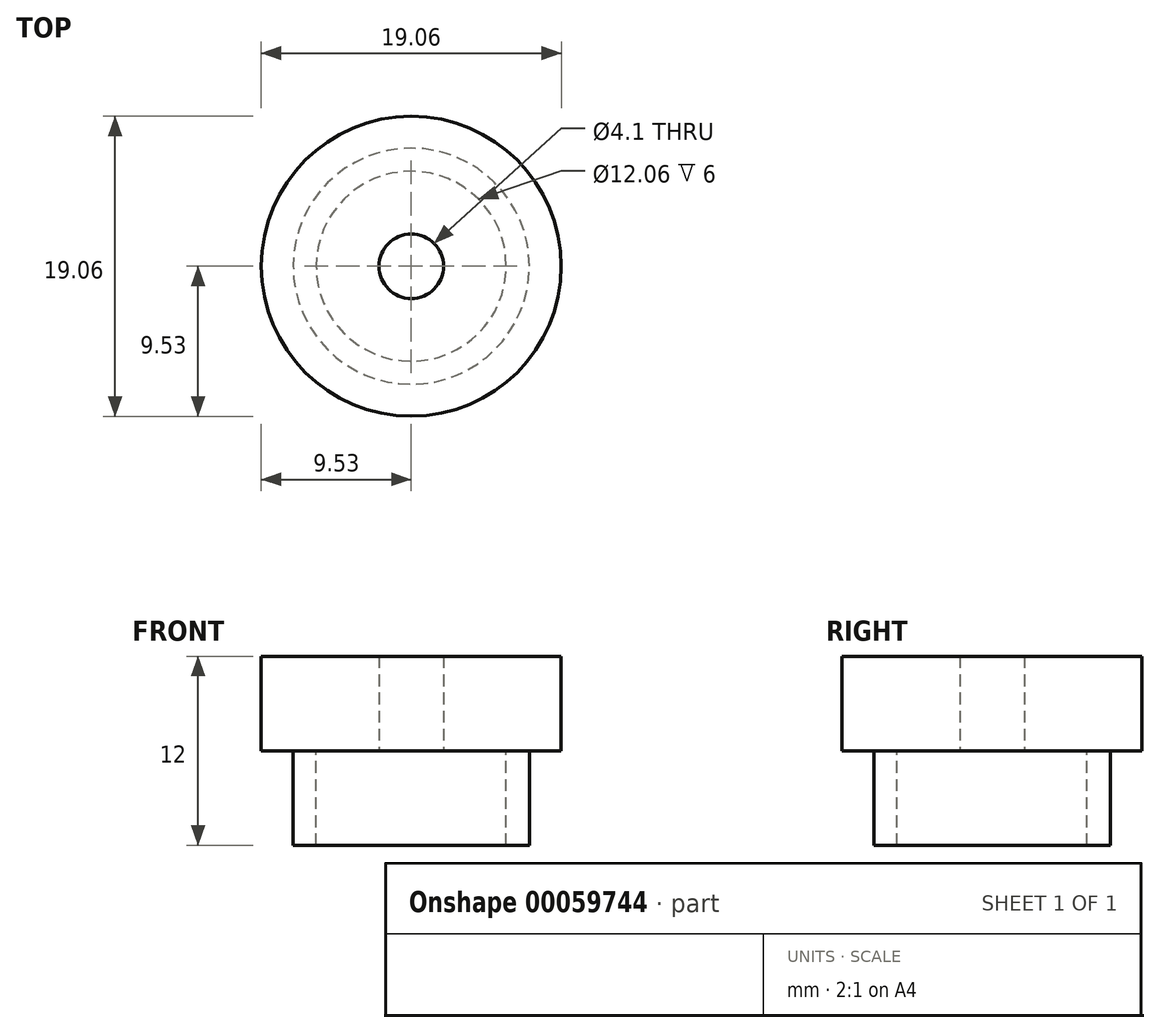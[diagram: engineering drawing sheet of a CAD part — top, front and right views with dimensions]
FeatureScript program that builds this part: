
annotation { "Feature Type Name" : "Feature", "Feature Type Description" : "" }
export const myFeature = defineFeature(function(context is Context, id is Id, definition is map)
    precondition{}
    {
        {
            var Q0;
            Q0=qCreatedBy(makeId("Top.planeOp"),FACE);
            var sketch = newSketch(context, id + "F0", { "sketchPlane" : qUnion([Q0])});
            skCircle(sketch, "E0", {"center": v(0, 0) * mm, "radius": 9.53 * mm});
            skCircle(sketch, "E1", {"center": v(0, 0) * mm, "radius": 7.5 * mm});
            skCircle(sketch, "E2", {"center": v(0, 0) * mm, "radius": 6.03 * mm});
            skCircle(sketch, "E3", {"center": v(0, 0) * mm, "radius": 2.05 * mm});
            skSolve(sketch);
        }
        {
            var Q0;
            Q0=makeQuery(id+"F0.imprint","IMPRINT",FACE,{"disambiguationData":[TD([[makeQuery(id+"F0.imprint","IMPRINT",EDGE,{"derivedFrom":sQuery(id+"F0.wireOp",EDGE,"E0")}),1.0]])]});
            var Q1;
            Q1=makeQuery(id+"F0.imprint","IMPRINT",FACE,{"disambiguationData":[TD([[makeQuery(id+"F0.imprint","IMPRINT",EDGE,{"derivedFrom":sQuery(id+"F0.wireOp",EDGE,"E1")}),1.0]])]});
            var Q2;
            Q2=makeQuery(id+"F0.imprint","IMPRINT",FACE,{"disambiguationData":[TD([[makeQuery(id+"F0.imprint","IMPRINT",EDGE,{"derivedFrom":sQuery(id+"F0.wireOp",EDGE,"E2")}),1.0]])]});
            extrude(context, id + "F1", {"entities" : qUnion([Q0, Q1, Q2]), "depth" : 6 * mm});
        }
        {
            var Q0;
            Q0=makeQuery(id+"F0.imprint","IMPRINT",FACE,{"disambiguationData":[TD([[makeQuery(id+"F0.imprint","IMPRINT",EDGE,{"derivedFrom":sQuery(id+"F0.wireOp",EDGE,"E1")}),1.0]])]});
            extrude(context, id + "F2", {"entities" : qUnion([Q0]), "operationType" : NewBodyOperationType.ADD, "oppositeDirection" : true, "depth" : 6 * mm});
        }
    });
